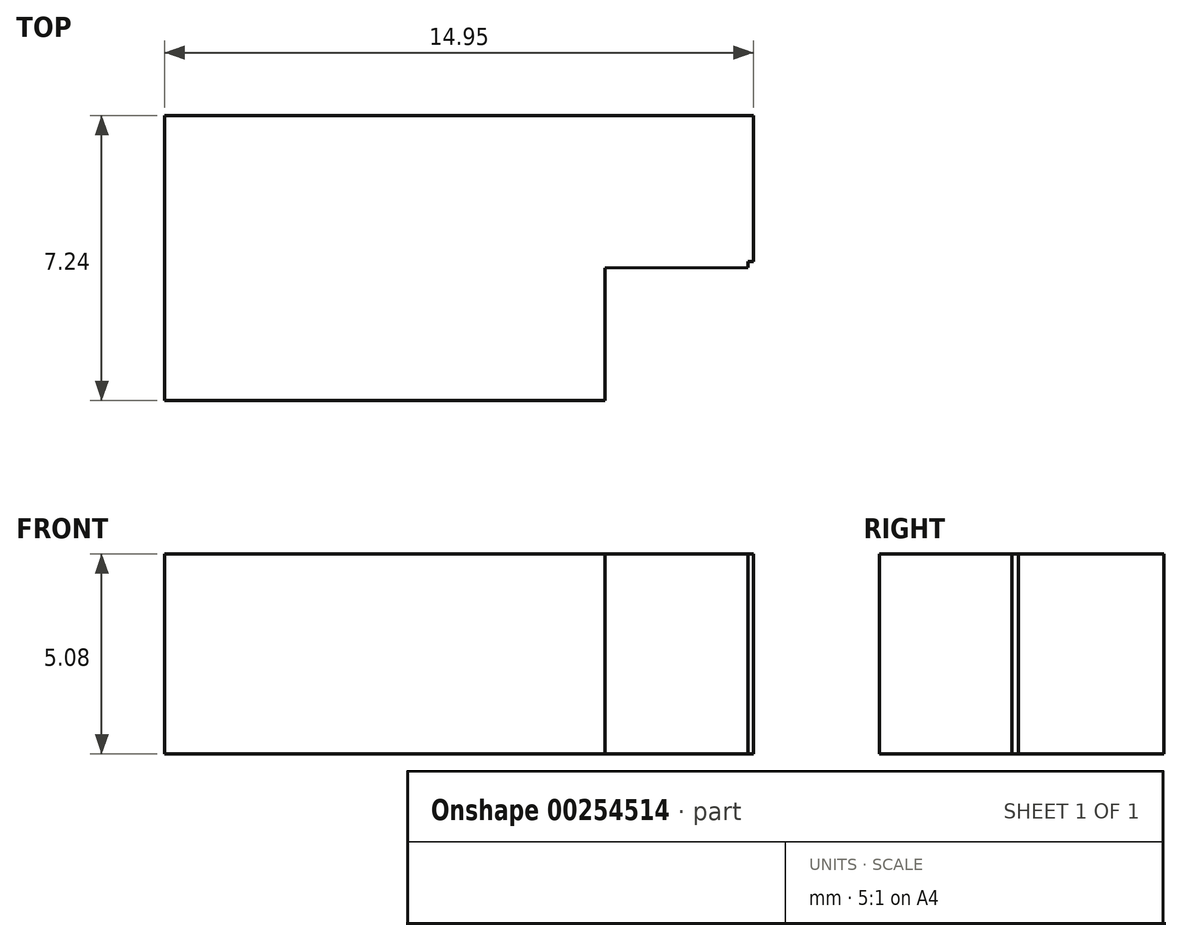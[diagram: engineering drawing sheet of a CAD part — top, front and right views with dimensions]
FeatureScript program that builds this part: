
annotation { "Feature Type Name" : "Feature", "Feature Type Description" : "" }
export const myFeature = defineFeature(function(context is Context, id is Id, definition is map)
    precondition{}
    {
        {
            var Q0;
            Q0=qCreatedBy(makeId("Top.planeOp"),FACE);
            var sketch = newSketch(context, id + "F0", { "sketchPlane" : qUnion([Q0])});
            skLineSegment(sketch, "E0", {"start": v(-33.45, 9.2) * mm, "end": v(-26.8, 16.12) * mm});
            skLineSegment(sketch, "E1", {"start": v(-26.8, 16.12) * mm, "end": v(-22.17, 16.12) * mm});
            skLineSegment(sketch, "E2", {"start": v(-22.17, 16.12) * mm, "end": v(-22.17, 19.99) * mm});
            skLineSegment(sketch, "E3", {"start": v(-22.17, 19.99) * mm, "end": v(-25.8, 19.97) * mm});
            skLineSegment(sketch, "E4", {"start": v(-25.8, 19.97) * mm, "end": v(-25.8, 38.73) * mm});
            skLineSegment(sketch, "E5", {"start": v(-25.8, 38.73) * mm, "end": v(-18.88, 45.9) * mm});
            skLineSegment(sketch, "E6", {"start": v(-18.88, 45.9) * mm, "end": v(14.3, 45.9) * mm});
            skLineSegment(sketch, "E7", {"start": v(14.3, 45.9) * mm, "end": v(22.2, 38.73) * mm});
            skLineSegment(sketch, "E8", {"start": v(22.2, 38.73) * mm, "end": v(22.2, 19.97) * mm});
            skLineSegment(sketch, "E9", {"start": v(22.2, 19.97) * mm, "end": v(18.52, 19.97) * mm});
            skLineSegment(sketch, "E10", {"start": v(18.52, 19.97) * mm, "end": v(18.52, 16.12) * mm});
            skLineSegment(sketch, "E11", {"start": v(18.52, 16.12) * mm, "end": v(22.2, 16.12) * mm});
            skLineSegment(sketch, "E12", {"start": v(22.2, 16.12) * mm, "end": v(29.83, 9.43) * mm});
            skLineSegment(sketch, "E13", {"start": v(29.83, 9.43) * mm, "end": v(29.83, -20.85) * mm});
            skLineSegment(sketch, "E14", {"start": v(29.83, -20.85) * mm, "end": v(22.14, -20.85) * mm});
            skLineSegment(sketch, "E15", {"start": v(22.14, -20.85) * mm, "end": v(22.14, -32.04) * mm});
            skLineSegment(sketch, "E16", {"start": v(22.14, -32.04) * mm, "end": v(19.03, -35.7) * mm});
            skLineSegment(sketch, "E17", {"start": v(19.03, -35.7) * mm, "end": v(3.87, -35.7) * mm});
            skLineSegment(sketch, "E18", {"start": v(3.87, -35.7) * mm, "end": v(3.87, -28.47) * mm});
            skLineSegment(sketch, "E19", {"start": v(3.87, -28.47) * mm, "end": v(-7.29, -28.47) * mm});
            skLineSegment(sketch, "E20", {"start": v(-7.29, -28.47) * mm, "end": v(-7.29, -35.7) * mm});
            skLineSegment(sketch, "E21", {"start": v(-7.29, -35.7) * mm, "end": v(-23.05, -35.7) * mm});
            skLineSegment(sketch, "E22", {"start": v(-23.05, -35.7) * mm, "end": v(-25.8, -32.44) * mm});
            skLineSegment(sketch, "E23", {"start": v(-25.8, -32.44) * mm, "end": v(-25.8, -20.85) * mm});
            skLineSegment(sketch, "E24", {"start": v(-25.8, -20.85) * mm, "end": v(-33.32, -20.85) * mm});
            skLineSegment(sketch, "E25", {"start": v(-33.32, -20.85) * mm, "end": v(-33.45, 9.2) * mm});
            skCircle(sketch, "E26", {"center": v(-11.3, 31.23) * mm, "radius": 5.9 * mm});
            skPoint(sketch, "E26.first.point", {"position": v(-17.19, 30.94) * mm});
            skPoint(sketch, "E26.second.point", {"position": v(-5.4, 31.07) * mm});
            skPoint(sketch, "E26.third.point", {"position": v(-11.26, 25.33) * mm});
            skCircle(sketch, "E27", {"center": v(7.12, 31) * mm, "radius": 5.64 * mm});
            skPoint(sketch, "E27.first.point", {"position": v(1.48, 30.84) * mm});
            skPoint(sketch, "E27.second.point", {"position": v(12.76, 30.78) * mm});
            skPoint(sketch, "E27.third.point", {"position": v(7.1, 36.64) * mm});
            skLineSegment(sketch, "E28.bottom", {"start": v(-14.96, 34.57) * mm, "end": v(-7.5, 34.57) * mm});
            skLineSegment(sketch, "E28.top", {"start": v(-14.96, 27.44) * mm, "end": v(-7.5, 27.44) * mm});
            skLineSegment(sketch, "E28.left", {"start": v(-14.96, 34.57) * mm, "end": v(-14.96, 27.44) * mm});
            skLineSegment(sketch, "E28.right", {"start": v(-7.5, 34.57) * mm, "end": v(-7.5, 27.44) * mm});
            skLineSegment(sketch, "E29.bottom", {"start": v(3.8, 34.28) * mm, "end": v(10.72, 34.28) * mm});
            skLineSegment(sketch, "E29.top", {"start": v(3.8, 27.44) * mm, "end": v(10.72, 27.44) * mm});
            skLineSegment(sketch, "E29.left", {"start": v(3.8, 34.28) * mm, "end": v(3.8, 27.44) * mm});
            skLineSegment(sketch, "E29.right", {"start": v(10.72, 34.28) * mm, "end": v(10.72, 27.44) * mm});
            skLineSegment(sketch, "E30.bottom", {"start": v(7.12, 31) * mm, "end": v(3.8, 31) * mm});
            skLineSegment(sketch, "E30.top", {"start": v(7.12, 34.28) * mm, "end": v(3.8, 34.28) * mm});
            skLineSegment(sketch, "E30.left", {"start": v(7.12, 31) * mm, "end": v(7.12, 34.28) * mm});
            skLineSegment(sketch, "E30.right", {"start": v(3.8, 31) * mm, "end": v(3.8, 34.28) * mm});
            skLineSegment(sketch, "E31.bottom", {"start": v(-11.3, 31.23) * mm, "end": v(-14.96, 31.23) * mm});
            skLineSegment(sketch, "E31.top", {"start": v(-11.3, 34.57) * mm, "end": v(-14.96, 34.57) * mm});
            skLineSegment(sketch, "E31.left", {"start": v(-11.3, 31.23) * mm, "end": v(-11.3, 34.57) * mm});
            skLineSegment(sketch, "E31.right", {"start": v(-14.96, 31.23) * mm, "end": v(-14.96, 34.57) * mm});
            skLineSegment(sketch, "E32.bottom", {"start": v(-3.8, 23.6) * mm, "end": v(0, 23.6) * mm});
            skLineSegment(sketch, "E32.top", {"start": v(-3.8, 19.8) * mm, "end": v(0, 19.8) * mm});
            skLineSegment(sketch, "E32.left", {"start": v(-3.8, 23.6) * mm, "end": v(-3.8, 19.8) * mm});
            skLineSegment(sketch, "E32.right", {"start": v(0, 23.6) * mm, "end": v(0, 19.8) * mm});
            skLineSegment(sketch, "E33.bottom", {"start": v(-7.5, 15.86) * mm, "end": v(3.8, 15.86) * mm});
            skLineSegment(sketch, "E33.top", {"start": v(-7.5, 12.27) * mm, "end": v(3.8, 12.27) * mm});
            skLineSegment(sketch, "E33.left", {"start": v(-7.5, 15.86) * mm, "end": v(-7.5, 12.27) * mm});
            skLineSegment(sketch, "E33.right", {"start": v(3.8, 15.86) * mm, "end": v(3.8, 12.27) * mm});
            skPoint(sketch, "E34.oppositeSnap0", {"position": v(-25.8, -26.64) * mm});
            skLineSegment(sketch, "E34.bottom", {"start": v(-29.45, -9.9) * mm, "end": v(-25.8, -9.9) * mm});
            skLineSegment(sketch, "E34.top", {"start": v(-29.45, -17.27) * mm, "end": v(-25.8, -17.27) * mm});
            skLineSegment(sketch, "E34.left", {"start": v(-29.45, -9.9) * mm, "end": v(-29.45, -17.27) * mm});
            skLineSegment(sketch, "E34.right", {"start": v(-25.8, -9.9) * mm, "end": v(-25.8, -17.27) * mm});
            skLineSegment(sketch, "E35.top", {"start": v(-29.45, 8.74) * mm, "end": v(-25.8, 8.74) * mm});
            skLineSegment(sketch, "E35.left", {"start": v(-29.45, -9.9) * mm, "end": v(-29.45, 8.74) * mm});
            skLineSegment(sketch, "E35.right", {"start": v(-25.8, -9.9) * mm, "end": v(-25.8, 8.74) * mm});
            skLineSegment(sketch, "E36.bottom", {"start": v(22.2, -9.9) * mm, "end": v(25.76, -9.9) * mm});
            skLineSegment(sketch, "E36.top", {"start": v(22.2, -17.27) * mm, "end": v(25.76, -17.27) * mm});
            skLineSegment(sketch, "E36.left", {"start": v(22.2, -9.9) * mm, "end": v(22.2, -17.27) * mm});
            skLineSegment(sketch, "E36.right", {"start": v(25.76, -9.9) * mm, "end": v(25.76, -17.27) * mm});
            skLineSegment(sketch, "E37.top", {"start": v(22.2, 8.7) * mm, "end": v(25.76, 8.7) * mm});
            skLineSegment(sketch, "E37.left", {"start": v(22.2, -9.9) * mm, "end": v(22.2, 8.7) * mm});
            skLineSegment(sketch, "E37.right", {"start": v(25.76, -9.9) * mm, "end": v(25.76, 8.7) * mm});
            skLineSegment(sketch, "E38.bottom", {"start": v(-3.6, -28.47) * mm, "end": v(0, -28.47) * mm});
            skLineSegment(sketch, "E38.top", {"start": v(-3.6, -24.74) * mm, "end": v(0, -24.74) * mm});
            skLineSegment(sketch, "E38.left", {"start": v(-3.6, -28.47) * mm, "end": v(-3.6, -24.74) * mm});
            skLineSegment(sketch, "E38.right", {"start": v(0, -28.47) * mm, "end": v(0, -24.74) * mm});
            skLineSegment(sketch, "E39", {"start": v(-22.24, -24.61) * mm, "end": v(-22.24, -31.85) * mm});
            skLineSegment(sketch, "E40", {"start": v(-22.24, -31.85) * mm, "end": v(-11.06, -31.85) * mm});
            skLineSegment(sketch, "E41", {"start": v(-11.06, -31.85) * mm, "end": v(-11.06, -28.48) * mm});
            skLineSegment(sketch, "E42", {"start": v(-11.06, -28.48) * mm, "end": v(-7.29, -28.47) * mm});
            skLineSegment(sketch, "E43", {"start": v(-7.29, -24.61) * mm, "end": v(-22.24, -24.61) * mm});
            skLineSegment(sketch, "E44", {"start": v(-7.29, -24.61) * mm, "end": v(-7.29, -28.47) * mm});
            skLineSegment(sketch, "E45", {"start": v(3.87, -28.47) * mm, "end": v(3.87, -24.61) * mm});
            skLineSegment(sketch, "E46", {"start": v(3.87, -24.61) * mm, "end": v(18.56, -24.61) * mm});
            skLineSegment(sketch, "E47", {"start": v(18.56, -24.61) * mm, "end": v(18.56, -31.97) * mm});
            skLineSegment(sketch, "E48", {"start": v(18.56, -31.97) * mm, "end": v(7.4, -31.97) * mm});
            skLineSegment(sketch, "E49", {"start": v(7.4, -31.97) * mm, "end": v(7.4, -28.47) * mm});
            skLineSegment(sketch, "E50", {"start": v(7.4, -28.47) * mm, "end": v(3.87, -28.47) * mm});
            skLineSegment(sketch, "E51", {"start": v(-22.17, 19.99) * mm, "end": v(-22.24, 38.23) * mm});
            skLineSegment(sketch, "E52", {"start": v(-22.24, 38.23) * mm, "end": v(-18.48, 38.25) * mm});
            skLineSegment(sketch, "E53", {"start": v(-18.48, 38.25) * mm, "end": v(-18.5, 42.04) * mm});
            skLineSegment(sketch, "E54", {"start": v(-18.5, 42.04) * mm, "end": v(14.76, 42.16) * mm});
            skLineSegment(sketch, "E55", {"start": v(14.76, 42.16) * mm, "end": v(14.78, 38.23) * mm});
            skLineSegment(sketch, "E56", {"start": v(14.78, 38.23) * mm, "end": v(18.52, 38.24) * mm});
            skLineSegment(sketch, "E57", {"start": v(18.52, 38.24) * mm, "end": v(18.52, 19.97) * mm});
            skLineSegment(sketch, "E58", {"start": v(3.8, 15.86) * mm, "end": v(3.8, 19.97) * mm});
            skLineSegment(sketch, "E59", {"start": v(3.8, 19.97) * mm, "end": v(18.52, 19.97) * mm});
            skLineSegment(sketch, "E60", {"start": v(-7.5, 15.86) * mm, "end": v(-7.5, 19.99) * mm});
            skLineSegment(sketch, "E61", {"start": v(-7.5, 19.99) * mm, "end": v(-22.17, 19.99) * mm});
            skLineSegment(sketch, "E62", {"start": v(-22.23, 12.38) * mm, "end": v(-22.23, -21.38) * mm});
            skLineSegment(sketch, "E63", {"start": v(-22.23, -21.38) * mm, "end": v(18.48, -21.38) * mm});
            skLineSegment(sketch, "E64", {"start": v(18.48, -21.38) * mm, "end": v(18.48, 12.34) * mm});
            skLineSegment(sketch, "E65", {"start": v(18.48, 12.34) * mm, "end": v(14.65, 12.34) * mm});
            skLineSegment(sketch, "E66", {"start": v(14.65, 12.34) * mm, "end": v(14.65, 15.86) * mm});
            skLineSegment(sketch, "E67", {"start": v(14.65, 15.86) * mm, "end": v(3.8, 15.86) * mm});
            skLineSegment(sketch, "E68", {"start": v(-22.23, 12.38) * mm, "end": v(-18.53, 12.38) * mm});
            skLineSegment(sketch, "E69", {"start": v(-18.53, 12.38) * mm, "end": v(-18.53, 15.86) * mm});
            skLineSegment(sketch, "E70", {"start": v(-18.53, 15.86) * mm, "end": v(-7.5, 15.86) * mm});
            skLineSegment(sketch, "E71.bottom", {"start": v(-7.42, -28.31) * mm, "end": v(-7.13, -28.31) * mm});
            skLineSegment(sketch, "E71.top", {"start": v(-7.42, -28.63) * mm, "end": v(-7.13, -28.63) * mm});
            skLineSegment(sketch, "E71.left", {"start": v(-7.42, -28.31) * mm, "end": v(-7.42, -28.63) * mm});
            skLineSegment(sketch, "E71.right", {"start": v(-7.13, -28.31) * mm, "end": v(-7.13, -28.63) * mm});
            skLineSegment(sketch, "E72.bottom", {"start": v(3.95, -28.38) * mm, "end": v(3.78, -28.38) * mm});
            skLineSegment(sketch, "E72.top", {"start": v(3.95, -28.56) * mm, "end": v(3.78, -28.56) * mm});
            skLineSegment(sketch, "E72.left", {"start": v(3.95, -28.38) * mm, "end": v(3.95, -28.56) * mm});
            skLineSegment(sketch, "E72.right", {"start": v(3.78, -28.38) * mm, "end": v(3.78, -28.56) * mm});
            skSolve(sketch);
        }
        {
            var Q0;
            Q0=makeQuery(id+"F0.imprint","IMPRINT",FACE,{"disambiguationData":[TD([[makeQuery(id+"F0.imprint","IMPRINT",EDGE,{"derivedFrom":sQuery(id+"F0.wireOp",EDGE,"E39")}),1.0]])]});
            extrude(context, id + "F1", {"entities" : qUnion([Q0]), "depth" : 5.08 * mm});
        }
    });
